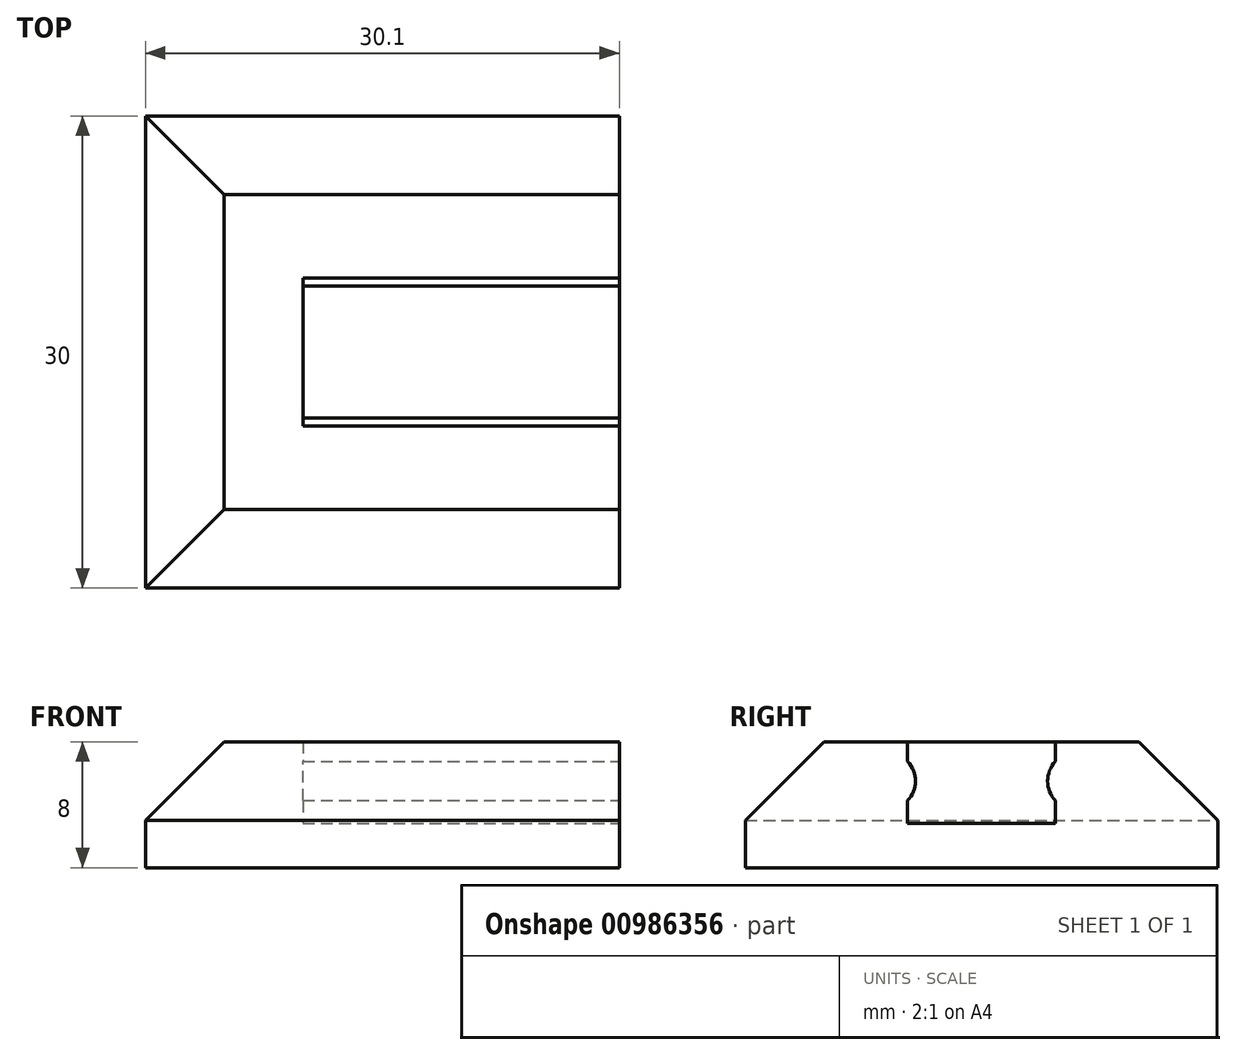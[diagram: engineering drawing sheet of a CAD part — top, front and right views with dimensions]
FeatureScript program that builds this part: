
annotation { "Feature Type Name" : "Feature", "Feature Type Description" : "" }
export const myFeature = defineFeature(function(context is Context, id is Id, definition is map)
    precondition{}
    {
        {
            var Q0;
            Q0=qCreatedBy(makeId("Top.planeOp"),FACE);
            var sketch = newSketch(context, id + "F0", { "sketchPlane" : qUnion([Q0])});
            skLineSegment(sketch, "E0.bottom", {"start": v(63.5, -4.5) * mm, "end": v(-26, -4.5) * mm});
            skLineSegment(sketch, "E0.top", {"start": v(63.5, 4.5) * mm, "end": v(-63.5, 4.5) * mm});
            skLineSegment(sketch, "E0.left", {"start": v(63.5, -4.5) * mm, "end": v(63.5, 4.5) * mm});
            skLineSegment(sketch, "E0.right", {"start": v(-63.5, -4.5) * mm, "end": v(-63.5, 4.5) * mm});
            skPoint(sketch, "E0.middle", {"position": v(0, 0) * mm});
            skLineSegment(sketch, "E1.0", {"start": v(8, 3) * mm, "end": v(-8, 3) * mm});
            skLineSegment(sketch, "E1.1", {"start": v(62, -3) * mm, "end": v(62, 3) * mm});
            skLineSegment(sketch, "E1.2", {"start": v(8, -3) * mm, "end": v(-8, -3) * mm});
            skLineSegment(sketch, "E1.3", {"start": v(-62, -3) * mm, "end": v(-62, 3) * mm});
            skLineSegment(sketch, "E2.left", {"start": v(8, -3) * mm, "end": v(8, 3) * mm, "construction": true});
            skLineSegment(sketch, "E2.right", {"start": v(-8, -3) * mm, "end": v(-8, 3) * mm, "construction": true});
            skLineSegment(sketch, "E3.top", {"start": v(-8, -4.5) * mm, "end": v(-10, -4.5) * mm});
            skLineSegment(sketch, "E3.left", {"start": v(-8, 3) * mm, "end": v(-8, -3) * mm});
            skLineSegment(sketch, "E3.right", {"start": v(-10, 3) * mm, "end": v(-10, -3) * mm});
            skLineSegment(sketch, "E4.top", {"start": v(-10, 4.5) * mm, "end": v(-26, 4.5) * mm, "construction": true});
            skLineSegment(sketch, "E4.left", {"start": v(-10, -3) * mm, "end": v(-10, 3) * mm, "construction": true});
            skLineSegment(sketch, "E4.right", {"start": v(-26, -3) * mm, "end": v(-26, 3) * mm, "construction": true});
            skLineSegment(sketch, "E5.bottom", {"start": v(-26, -4.5) * mm, "end": v(-28, -4.5) * mm});
            skLineSegment(sketch, "E5.top", {"start": v(-26, 4.5) * mm, "end": v(-28, 4.5) * mm});
            skLineSegment(sketch, "E5.left", {"start": v(-26, -3) * mm, "end": v(-26, 3) * mm});
            skLineSegment(sketch, "E5.right", {"start": v(-28, -3) * mm, "end": v(-28, 3) * mm});
            skLineSegment(sketch, "E6.top", {"start": v(-28, 4.5) * mm, "end": v(-44, 4.5) * mm, "construction": true});
            skLineSegment(sketch, "E6.left", {"start": v(-28, -3) * mm, "end": v(-28, 3) * mm, "construction": true});
            skLineSegment(sketch, "E6.right", {"start": v(-44, -3) * mm, "end": v(-44, 3) * mm, "construction": true});
            skLineSegment(sketch, "E7.top", {"start": v(-44, 4.5) * mm, "end": v(-46, 4.5) * mm});
            skLineSegment(sketch, "E7.left", {"start": v(-44, -3) * mm, "end": v(-44, 3) * mm});
            skLineSegment(sketch, "E7.right", {"start": v(-46, -3) * mm, "end": v(-46, 3) * mm});
            skLineSegment(sketch, "E8.top", {"start": v(-46, 4.5) * mm, "end": v(-62, 4.5) * mm, "construction": true});
            skLineSegment(sketch, "E8.left", {"start": v(-46, -3) * mm, "end": v(-46, 3) * mm, "construction": true});
            skLineSegment(sketch, "E8.right", {"start": v(-62, -5) * mm, "end": v(-62, -4.5) * mm, "construction": true});
            skLineSegment(sketch, "E9.trimOffspring", {"start": v(-28, 3) * mm, "end": v(-44, 3) * mm});
            skLineSegment(sketch, "E10.trimOffspring", {"start": v(-46, 3) * mm, "end": v(-62, 3) * mm});
            skLineSegment(sketch, "E11.trimOffspring", {"start": v(-46, -3) * mm, "end": v(-62, -3) * mm});
            skLineSegment(sketch, "E12.trimOffspring", {"start": v(-28, -4.5) * mm, "end": v(-63.5, -4.5) * mm});
            skLineSegment(sketch, "E13.trimOffspring", {"start": v(-28, -3) * mm, "end": v(-44, -3) * mm});
            skLineSegment(sketch, "E14.trimOffspring", {"start": v(-10, 3) * mm, "end": v(-26, 3) * mm});
            skLineSegment(sketch, "E15.trimOffspring", {"start": v(-10, -3) * mm, "end": v(-26, -3) * mm});
            skLineSegment(sketch, "E16", {"start": v(0, 11.85) * mm, "end": v(0, -12.1) * mm, "construction": true});
            skLineSegment(sketch, "E17.MirrorCS", {"start": v(-8, 3) * mm, "end": v(8, 3) * mm});
            skLineSegment(sketch, "E18.MirrorCS", {"start": v(-8, -3) * mm, "end": v(8, -3) * mm});
            skLineSegment(sketch, "E19.MirrorCS", {"start": v(10, -3) * mm, "end": v(10, 3) * mm, "construction": true});
            skLineSegment(sketch, "E20.MirrorCS", {"start": v(10, 3) * mm, "end": v(26, 3) * mm});
            skLineSegment(sketch, "E21.MirrorCS", {"start": v(10, -3) * mm, "end": v(26, -3) * mm});
            skLineSegment(sketch, "E22.MirrorCS", {"start": v(26, -3) * mm, "end": v(26, 3) * mm, "construction": true});
            skLineSegment(sketch, "E23.MirrorCS", {"start": v(28, -3) * mm, "end": v(28, 3) * mm, "construction": true});
            skLineSegment(sketch, "E24.MirrorCS", {"start": v(28, 3) * mm, "end": v(44, 3) * mm});
            skLineSegment(sketch, "E25.MirrorCS", {"start": v(28, -3) * mm, "end": v(44, -3) * mm});
            skLineSegment(sketch, "E26.MirrorCS", {"start": v(46, -3) * mm, "end": v(62, -3) * mm});
            skLineSegment(sketch, "E27.MirrorCS", {"start": v(46, 3) * mm, "end": v(62, 3) * mm});
            skLineSegment(sketch, "E28.MirrorCS", {"start": v(46, -3) * mm, "end": v(46, 3) * mm, "construction": true});
            skLineSegment(sketch, "E29.MirrorCS", {"start": v(44, -3) * mm, "end": v(44, 3) * mm, "construction": true});
            skLineSegment(sketch, "E30", {"start": v(10, 3) * mm, "end": v(10, -3) * mm});
            skLineSegment(sketch, "E31", {"start": v(26, 3) * mm, "end": v(26, -3) * mm});
            skLineSegment(sketch, "E32", {"start": v(28, 3) * mm, "end": v(28, -3) * mm});
            skLineSegment(sketch, "E33", {"start": v(44, 3) * mm, "end": v(44, -3) * mm});
            skLineSegment(sketch, "E34", {"start": v(46, 3) * mm, "end": v(46, -3) * mm});
            skLineSegment(sketch, "E35", {"start": v(8, 3) * mm, "end": v(8, -3) * mm});
            skPoint(sketch, "E36.orphan", {"position": v(-8, -6) * mm});
            skPoint(sketch, "E2.bottom.start.orphan", {"position": v(8, -6) * mm});
            skPoint(sketch, "E37.orphan", {"position": v(8, 6) * mm});
            skPoint(sketch, "E3.bottom.start.orphan", {"position": v(-8, 6) * mm});
            skSolve(sketch);
        }
        {
            var Q0;
            {var subQ6=sQuery(id+"F0.wireOp",EDGE,"E0.left");Q0=makeQuery(id+"F0.imprint","IMPRINT",FACE,{"disambiguationData":[TD([[makeQuery(id+"F0.imprint","IMPRINT",EDGE,{"derivedFrom":subQ6}),1.0]])]});}
            extrude(context, id + "F1", {"entities" : qUnion([Q0]), "depth" : 95 * mm, "offsetDistance" : 25 * mm});
        }
        {
            var Q0;
            Q0=makeQuery(id+"F0.imprint","IMPRINT",FACE,{"disambiguationData":[TD([[makeQuery(id+"F0.imprint","IMPRINT",EDGE,{"derivedFrom":sQuery(id+"F0.wireOp",EDGE,"E1.3")}),-1.0]])]});
            var Q1;
            Q1=makeQuery(id+"F0.imprint","IMPRINT",FACE,{"disambiguationData":[TD([[makeQuery(id+"F0.imprint","IMPRINT",EDGE,{"derivedFrom":sQuery(id+"F0.wireOp",EDGE,"E5.right")}),1.0]])]});
            var Q2;
            {var subQ6=sQuery(id+"F0.wireOp",EDGE,"E0.left");Q2=makeQuery(id+"F0.imprint","IMPRINT",FACE,{"disambiguationData":[TD([[makeQuery(id+"F0.imprint","IMPRINT",EDGE,{"derivedFrom":subQ6}),1.0]])]});}
            var Q3;
            Q3=makeQuery(id+"F0.imprint","IMPRINT",FACE,{"disambiguationData":[TD([[makeQuery(id+"F0.imprint","IMPRINT",EDGE,{"derivedFrom":sQuery(id+"F0.wireOp",EDGE,"E3.right")}),-1.0]])]});
            var Q4;
            Q4=makeQuery(id+"F0.imprint","IMPRINT",FACE,{"disambiguationData":[TD([[makeQuery(id+"F0.imprint","IMPRINT",EDGE,{"derivedFrom":sQuery(id+"F0.wireOp",EDGE,"E3.left")}),1.0]])]});
            var Q5;
            Q5=makeQuery(id+"F0.imprint","IMPRINT",FACE,{"disambiguationData":[TD([[makeQuery(id+"F0.imprint","IMPRINT",EDGE,{"derivedFrom":sQuery(id+"F0.wireOp",EDGE,"E20.MirrorCS")}),-1.0]])]});
            var Q6;
            Q6=makeQuery(id+"F0.imprint","IMPRINT",FACE,{"disambiguationData":[TD([[makeQuery(id+"F0.imprint","IMPRINT",EDGE,{"derivedFrom":sQuery(id+"F0.wireOp",EDGE,"E24.MirrorCS")}),-1.0]])]});
            var Q7;
            Q7=makeQuery(id+"F0.imprint","IMPRINT",FACE,{"disambiguationData":[TD([[makeQuery(id+"F0.imprint","IMPRINT",EDGE,{"derivedFrom":sQuery(id+"F0.wireOp",EDGE,"E26.MirrorCS")}),1.0]])]});
            extrude(context, id + "F2", {"entities" : qUnion([Q0, Q1, Q2, Q3, Q4, Q5, Q6, Q7]), "operationType" : NewBodyOperationType.ADD, "oppositeDirection" : true, "depth" : 5 * mm, "offsetDistance" : 25 * mm});
        }
        {
            var Q0;
            {var subQ0=sQuery(id+"F0.wireOp",EDGE,"E0.right");Q0=makeQuery(id+"F2.boolean.opBoolean","MERGE",FACE,{"derivedFrom":[makeQuery(id+"F1.opExtrude","SWEPT_FACE",FACE,{"disambiguationData":[OSD([subQ0])]}),makeQuery(id+"F2.opExtrude","SWEPT_FACE",FACE,{"disambiguationData":[OSD([subQ0])]})]});}
            var sketch = newSketch(context, id + "F3", { "sketchPlane" : qUnion([Q0])});
            skLineSegment(sketch, "E38", {"start": v(0, 0) * mm, "end": v(0, -7.08) * mm, "construction": true});
            skLineSegment(sketch, "E39", {"start": v(-6.2, -2.5) * mm, "end": v(6.74, -2.5) * mm, "construction": true});
            skCircle(sketch, "E40", {"center": v(-6, -2.5) * mm, "radius": 2 * mm});
            skCircle(sketch, "E41.MirrorC", {"center": v(6, -2.5) * mm, "radius": 2 * mm});
            skSolve(sketch);
        }
        {
            var Q0;
            Q0=qSketchRegion(id+"F3",true);
            extrude(context, id + "F4", {"entities" : qUnion([Q0]), "operationType" : NewBodyOperationType.REMOVE, "endBound" : BoundingType.THROUGH_ALL, "oppositeDirection" : true, "depth" : 25 * mm, "offsetDistance" : 25 * mm});
        }
        {
            var Q0;
            {var subQ0=sQuery(id+"F0.wireOp",EDGE,"E7.top");var subQ1=sQuery(id+"F0.wireOp",EDGE,"E5.top");var subQ2=sQuery(id+"F0.wireOp",EDGE,"E0.top");var subQ3=sQuery(id+"F0.wireOp",EDGE,"E0.right");Q0=makeQuery(id+"F4.boolean.opBoolean","SPLIT",EDGE,{"disambiguationData":[TD([makeQuery(id+"F1.opExtrude","CAP_FACE",FACE,{"disambiguationData":[OSD([sQuery(id+"F0.wireOp",EDGE,"E0.bottom"),subQ2,sQuery(id+"F0.wireOp",EDGE,"E0.left"),subQ3,sQuery(id+"F0.wireOp",EDGE,"E1.3"),sQuery(id+"F0.wireOp",EDGE,"E3.top"),sQuery(id+"F0.wireOp",EDGE,"E3.left"),sQuery(id+"F0.wireOp",EDGE,"E3.right"),sQuery(id+"F0.wireOp",EDGE,"E5.bottom"),subQ1,sQuery(id+"F0.wireOp",EDGE,"E5.left"),sQuery(id+"F0.wireOp",EDGE,"E5.right"),subQ0,sQuery(id+"F0.wireOp",EDGE,"E7.left"),sQuery(id+"F0.wireOp",EDGE,"E7.right"),sQuery(id+"F0.wireOp",EDGE,"E9.trimOffspring"),sQuery(id+"F0.wireOp",EDGE,"E10.trimOffspring"),sQuery(id+"F0.wireOp",EDGE,"E11.trimOffspring"),sQuery(id+"F0.wireOp",EDGE,"E12.trimOffspring"),sQuery(id+"F0.wireOp",EDGE,"E13.trimOffspring"),sQuery(id+"F0.wireOp",EDGE,"E14.trimOffspring"),sQuery(id+"F0.wireOp",EDGE,"E15.trimOffspring"),sQuery(id+"F0.wireOp",EDGE,"E17.MirrorCS"),sQuery(id+"F0.wireOp",EDGE,"E18.MirrorCS"),sQuery(id+"F0.wireOp",EDGE,"E20.MirrorCS"),sQuery(id+"F0.wireOp",EDGE,"E21.MirrorCS"),sQuery(id+"F0.wireOp",EDGE,"E24.MirrorCS"),sQuery(id+"F0.wireOp",EDGE,"E25.MirrorCS"),sQuery(id+"F0.wireOp",EDGE,"E26.MirrorCS"),sQuery(id+"F0.wireOp",EDGE,"E27.MirrorCS"),sQuery(id+"F0.wireOp",EDGE,"E1.1"),sQuery(id+"F0.wireOp",EDGE,"E30"),sQuery(id+"F0.wireOp",EDGE,"E31"),sQuery(id+"F0.wireOp",EDGE,"E32"),sQuery(id+"F0.wireOp",EDGE,"E33"),sQuery(id+"F0.wireOp",EDGE,"E34"),sQuery(id+"F0.wireOp",EDGE,"E35")])],"isStart":false})])],"derivedFrom":makeQuery(id+"F2.boolean.opBoolean","MERGE",EDGE,{"derivedFrom":[makeQuery(id+"F1.opExtrude","SWEPT_EDGE",EDGE,{"disambiguationData":[OSD([subQ2,subQ3])]}),makeQuery(id+"F2.opExtrude","SWEPT_EDGE",EDGE,{"disambiguationData":[OSD([subQ2,subQ3])]})]})});}
            var Q1;
            {var subQ0=sQuery(id+"F0.wireOp",EDGE,"E12.trimOffspring");var subQ1=sQuery(id+"F0.wireOp",EDGE,"E5.bottom");var subQ2=sQuery(id+"F0.wireOp",EDGE,"E3.top");var subQ3=sQuery(id+"F0.wireOp",EDGE,"E0.bottom");var subQ4=sQuery(id+"F0.wireOp",EDGE,"E0.right");Q1=makeQuery(id+"F4.boolean.opBoolean","SPLIT",EDGE,{"disambiguationData":[TD([makeQuery(id+"F1.opExtrude","CAP_FACE",FACE,{"disambiguationData":[OSD([subQ3,sQuery(id+"F0.wireOp",EDGE,"E0.top"),sQuery(id+"F0.wireOp",EDGE,"E0.left"),subQ4,sQuery(id+"F0.wireOp",EDGE,"E1.3"),subQ2,sQuery(id+"F0.wireOp",EDGE,"E3.left"),sQuery(id+"F0.wireOp",EDGE,"E3.right"),subQ1,sQuery(id+"F0.wireOp",EDGE,"E5.top"),sQuery(id+"F0.wireOp",EDGE,"E5.left"),sQuery(id+"F0.wireOp",EDGE,"E5.right"),sQuery(id+"F0.wireOp",EDGE,"E7.top"),sQuery(id+"F0.wireOp",EDGE,"E7.left"),sQuery(id+"F0.wireOp",EDGE,"E7.right"),sQuery(id+"F0.wireOp",EDGE,"E9.trimOffspring"),sQuery(id+"F0.wireOp",EDGE,"E10.trimOffspring"),sQuery(id+"F0.wireOp",EDGE,"E11.trimOffspring"),subQ0,sQuery(id+"F0.wireOp",EDGE,"E13.trimOffspring"),sQuery(id+"F0.wireOp",EDGE,"E14.trimOffspring"),sQuery(id+"F0.wireOp",EDGE,"E15.trimOffspring"),sQuery(id+"F0.wireOp",EDGE,"E17.MirrorCS"),sQuery(id+"F0.wireOp",EDGE,"E18.MirrorCS"),sQuery(id+"F0.wireOp",EDGE,"E20.MirrorCS"),sQuery(id+"F0.wireOp",EDGE,"E21.MirrorCS"),sQuery(id+"F0.wireOp",EDGE,"E24.MirrorCS"),sQuery(id+"F0.wireOp",EDGE,"E25.MirrorCS"),sQuery(id+"F0.wireOp",EDGE,"E26.MirrorCS"),sQuery(id+"F0.wireOp",EDGE,"E27.MirrorCS"),sQuery(id+"F0.wireOp",EDGE,"E1.1"),sQuery(id+"F0.wireOp",EDGE,"E30"),sQuery(id+"F0.wireOp",EDGE,"E31"),sQuery(id+"F0.wireOp",EDGE,"E32"),sQuery(id+"F0.wireOp",EDGE,"E33"),sQuery(id+"F0.wireOp",EDGE,"E34"),sQuery(id+"F0.wireOp",EDGE,"E35")])],"isStart":false})])],"derivedFrom":makeQuery(id+"F2.boolean.opBoolean","MERGE",EDGE,{"derivedFrom":[makeQuery(id+"F1.opExtrude","SWEPT_EDGE",EDGE,{"disambiguationData":[OSD([subQ4,subQ0])]}),makeQuery(id+"F2.opExtrude","SWEPT_EDGE",EDGE,{"disambiguationData":[OSD([subQ4,subQ0])]})]})});}
            var Q2;
            Q2=makeQuery(id+"F2.opExtrude","CAP_EDGE",EDGE,{"disambiguationData":[OSD([sQuery(id+"F0.wireOp",EDGE,"E0.top"),sQuery(id+"F0.wireOp",EDGE,"E5.top"),sQuery(id+"F0.wireOp",EDGE,"E7.top")])],"isStart":false});
            var Q3;
            Q3=makeQuery(id+"F2.opExtrude","CAP_EDGE",EDGE,{"disambiguationData":[OSD([sQuery(id+"F0.wireOp",EDGE,"E0.right")])],"isStart":false});
            var Q4;
            Q4=makeQuery(id+"F4.boolean.opBoolean","COPY",EDGE,{"derivedFrom":makeQuery(id+"F4.opExtrude","CAP_EDGE",EDGE,{"disambiguationData":[OSD([sQuery(id+"F3.wireOp",EDGE,"E40")])],"isStart":true})});
            var Q5;
            Q5=makeQuery(id+"F1.opExtrude","CAP_EDGE",EDGE,{"disambiguationData":[OSD([sQuery(id+"F0.wireOp",EDGE,"E0.top"),sQuery(id+"F0.wireOp",EDGE,"E5.top"),sQuery(id+"F0.wireOp",EDGE,"E7.top")])],"isStart":false});
            var Q6;
            Q6=makeQuery(id+"F1.opExtrude","CAP_EDGE",EDGE,{"disambiguationData":[OSD([sQuery(id+"F0.wireOp",EDGE,"E0.right")])],"isStart":false});
            var Q7;
            Q7=makeQuery(id+"F1.opExtrude","CAP_EDGE",EDGE,{"disambiguationData":[OSD([sQuery(id+"F0.wireOp",EDGE,"E0.bottom"),sQuery(id+"F0.wireOp",EDGE,"E3.top"),sQuery(id+"F0.wireOp",EDGE,"E5.bottom"),sQuery(id+"F0.wireOp",EDGE,"E12.trimOffspring")])],"isStart":false});
            var Q8;
            Q8=makeQuery(id+"F1.opExtrude","CAP_EDGE",EDGE,{"disambiguationData":[OSD([sQuery(id+"F0.wireOp",EDGE,"E0.left")])],"isStart":false});
            var Q9;
            Q9=makeQuery(id+"F2.opExtrude","CAP_EDGE",EDGE,{"disambiguationData":[OSD([sQuery(id+"F0.wireOp",EDGE,"E0.left")])],"isStart":false});
            var Q10;
            {var subQ0=sQuery(id+"F0.wireOp",EDGE,"E7.top");var subQ1=sQuery(id+"F0.wireOp",EDGE,"E5.top");var subQ2=sQuery(id+"F0.wireOp",EDGE,"E0.top");var subQ3=sQuery(id+"F0.wireOp",EDGE,"E0.left");Q10=makeQuery(id+"F4.boolean.opBoolean","SPLIT",EDGE,{"disambiguationData":[TD([makeQuery(id+"F1.opExtrude","CAP_FACE",FACE,{"disambiguationData":[OSD([sQuery(id+"F0.wireOp",EDGE,"E0.bottom"),subQ2,subQ3,sQuery(id+"F0.wireOp",EDGE,"E0.right"),sQuery(id+"F0.wireOp",EDGE,"E1.3"),sQuery(id+"F0.wireOp",EDGE,"E3.top"),sQuery(id+"F0.wireOp",EDGE,"E3.left"),sQuery(id+"F0.wireOp",EDGE,"E3.right"),sQuery(id+"F0.wireOp",EDGE,"E5.bottom"),subQ1,sQuery(id+"F0.wireOp",EDGE,"E5.left"),sQuery(id+"F0.wireOp",EDGE,"E5.right"),subQ0,sQuery(id+"F0.wireOp",EDGE,"E7.left"),sQuery(id+"F0.wireOp",EDGE,"E7.right"),sQuery(id+"F0.wireOp",EDGE,"E9.trimOffspring"),sQuery(id+"F0.wireOp",EDGE,"E10.trimOffspring"),sQuery(id+"F0.wireOp",EDGE,"E11.trimOffspring"),sQuery(id+"F0.wireOp",EDGE,"E12.trimOffspring"),sQuery(id+"F0.wireOp",EDGE,"E13.trimOffspring"),sQuery(id+"F0.wireOp",EDGE,"E14.trimOffspring"),sQuery(id+"F0.wireOp",EDGE,"E15.trimOffspring"),sQuery(id+"F0.wireOp",EDGE,"E17.MirrorCS"),sQuery(id+"F0.wireOp",EDGE,"E18.MirrorCS"),sQuery(id+"F0.wireOp",EDGE,"E20.MirrorCS"),sQuery(id+"F0.wireOp",EDGE,"E21.MirrorCS"),sQuery(id+"F0.wireOp",EDGE,"E24.MirrorCS"),sQuery(id+"F0.wireOp",EDGE,"E25.MirrorCS"),sQuery(id+"F0.wireOp",EDGE,"E26.MirrorCS"),sQuery(id+"F0.wireOp",EDGE,"E27.MirrorCS"),sQuery(id+"F0.wireOp",EDGE,"E1.1"),sQuery(id+"F0.wireOp",EDGE,"E30"),sQuery(id+"F0.wireOp",EDGE,"E31"),sQuery(id+"F0.wireOp",EDGE,"E32"),sQuery(id+"F0.wireOp",EDGE,"E33"),sQuery(id+"F0.wireOp",EDGE,"E34"),sQuery(id+"F0.wireOp",EDGE,"E35")])],"isStart":false})])],"derivedFrom":makeQuery(id+"F2.boolean.opBoolean","MERGE",EDGE,{"derivedFrom":[makeQuery(id+"F1.opExtrude","SWEPT_EDGE",EDGE,{"disambiguationData":[OSD([subQ2,subQ3])]}),makeQuery(id+"F2.opExtrude","SWEPT_EDGE",EDGE,{"disambiguationData":[OSD([subQ2,subQ3])]})]})});}
            var Q11;
            {var subQ0=sQuery(id+"F0.wireOp",EDGE,"E12.trimOffspring");var subQ1=sQuery(id+"F0.wireOp",EDGE,"E5.bottom");var subQ2=sQuery(id+"F0.wireOp",EDGE,"E3.top");var subQ3=sQuery(id+"F0.wireOp",EDGE,"E0.bottom");var subQ4=sQuery(id+"F0.wireOp",EDGE,"E0.left");Q11=makeQuery(id+"F4.boolean.opBoolean","SPLIT",EDGE,{"disambiguationData":[TD([makeQuery(id+"F1.opExtrude","CAP_FACE",FACE,{"disambiguationData":[OSD([subQ3,sQuery(id+"F0.wireOp",EDGE,"E0.top"),subQ4,sQuery(id+"F0.wireOp",EDGE,"E0.right"),sQuery(id+"F0.wireOp",EDGE,"E1.3"),subQ2,sQuery(id+"F0.wireOp",EDGE,"E3.left"),sQuery(id+"F0.wireOp",EDGE,"E3.right"),subQ1,sQuery(id+"F0.wireOp",EDGE,"E5.top"),sQuery(id+"F0.wireOp",EDGE,"E5.left"),sQuery(id+"F0.wireOp",EDGE,"E5.right"),sQuery(id+"F0.wireOp",EDGE,"E7.top"),sQuery(id+"F0.wireOp",EDGE,"E7.left"),sQuery(id+"F0.wireOp",EDGE,"E7.right"),sQuery(id+"F0.wireOp",EDGE,"E9.trimOffspring"),sQuery(id+"F0.wireOp",EDGE,"E10.trimOffspring"),sQuery(id+"F0.wireOp",EDGE,"E11.trimOffspring"),subQ0,sQuery(id+"F0.wireOp",EDGE,"E13.trimOffspring"),sQuery(id+"F0.wireOp",EDGE,"E14.trimOffspring"),sQuery(id+"F0.wireOp",EDGE,"E15.trimOffspring"),sQuery(id+"F0.wireOp",EDGE,"E17.MirrorCS"),sQuery(id+"F0.wireOp",EDGE,"E18.MirrorCS"),sQuery(id+"F0.wireOp",EDGE,"E20.MirrorCS"),sQuery(id+"F0.wireOp",EDGE,"E21.MirrorCS"),sQuery(id+"F0.wireOp",EDGE,"E24.MirrorCS"),sQuery(id+"F0.wireOp",EDGE,"E25.MirrorCS"),sQuery(id+"F0.wireOp",EDGE,"E26.MirrorCS"),sQuery(id+"F0.wireOp",EDGE,"E27.MirrorCS"),sQuery(id+"F0.wireOp",EDGE,"E1.1"),sQuery(id+"F0.wireOp",EDGE,"E30"),sQuery(id+"F0.wireOp",EDGE,"E31"),sQuery(id+"F0.wireOp",EDGE,"E32"),sQuery(id+"F0.wireOp",EDGE,"E33"),sQuery(id+"F0.wireOp",EDGE,"E34"),sQuery(id+"F0.wireOp",EDGE,"E35")])],"isStart":false})])],"derivedFrom":makeQuery(id+"F2.boolean.opBoolean","MERGE",EDGE,{"derivedFrom":[makeQuery(id+"F1.opExtrude","SWEPT_EDGE",EDGE,{"disambiguationData":[OSD([subQ3,subQ4])]}),makeQuery(id+"F2.opExtrude","SWEPT_EDGE",EDGE,{"disambiguationData":[OSD([subQ3,subQ4])]})]})});}
            var Q12;
            Q12=makeQuery(id+"F4.boolean.opBoolean","COPY",EDGE,{"derivedFrom":makeQuery(id+"F4.opExtrude","CAP_EDGE",EDGE,{"disambiguationData":[OSD([sQuery(id+"F3.wireOp",EDGE,"E41.MirrorC")])],"isStart":true})});
            var Q13;
            {var subQ0=sQuery(id+"F0.wireOp",EDGE,"E0.left");Q13=makeQuery(id+"F4.boolean.opBoolean","INTERSECT",EDGE,{"derivedFrom":[makeQuery(id+"F2.boolean.opBoolean","MERGE",FACE,{"derivedFrom":[makeQuery(id+"F1.opExtrude","SWEPT_FACE",FACE,{"disambiguationData":[OSD([subQ0])]}),makeQuery(id+"F2.opExtrude","SWEPT_FACE",FACE,{"disambiguationData":[OSD([subQ0])]})]}),makeQuery(id+"F4.opExtrude","SWEPT_FACE",FACE,{"disambiguationData":[OSD([sQuery(id+"F3.wireOp",EDGE,"E40")])]})]});}
            var Q14;
            {var subQ0=sQuery(id+"F0.wireOp",EDGE,"E0.left");Q14=makeQuery(id+"F4.boolean.opBoolean","INTERSECT",EDGE,{"derivedFrom":[makeQuery(id+"F2.boolean.opBoolean","MERGE",FACE,{"derivedFrom":[makeQuery(id+"F1.opExtrude","SWEPT_FACE",FACE,{"disambiguationData":[OSD([subQ0])]}),makeQuery(id+"F2.opExtrude","SWEPT_FACE",FACE,{"disambiguationData":[OSD([subQ0])]})]}),makeQuery(id+"F4.opExtrude","SWEPT_FACE",FACE,{"disambiguationData":[OSD([sQuery(id+"F3.wireOp",EDGE,"E41.MirrorC")])]})]});}
            var Q15;
            Q15=makeQuery(id+"F1.opExtrude","CAP_EDGE",EDGE,{"disambiguationData":[OSD([sQuery(id+"F0.wireOp",EDGE,"E26.MirrorCS")])],"isStart":false});
            var Q16;
            Q16=makeQuery(id+"F1.opExtrude","CAP_EDGE",EDGE,{"disambiguationData":[OSD([sQuery(id+"F0.wireOp",EDGE,"E34")])],"isStart":false});
            var Q17;
            Q17=makeQuery(id+"F1.opExtrude","CAP_EDGE",EDGE,{"disambiguationData":[OSD([sQuery(id+"F0.wireOp",EDGE,"E27.MirrorCS")])],"isStart":false});
            var Q18;
            Q18=makeQuery(id+"F1.opExtrude","CAP_EDGE",EDGE,{"disambiguationData":[OSD([sQuery(id+"F0.wireOp",EDGE,"E1.1")])],"isStart":false});
            var Q19;
            Q19=makeQuery(id+"F1.opExtrude","CAP_EDGE",EDGE,{"disambiguationData":[OSD([sQuery(id+"F0.wireOp",EDGE,"E33")])],"isStart":false});
            var Q20;
            Q20=makeQuery(id+"F1.opExtrude","CAP_EDGE",EDGE,{"disambiguationData":[OSD([sQuery(id+"F0.wireOp",EDGE,"E24.MirrorCS")])],"isStart":false});
            var Q21;
            Q21=makeQuery(id+"F1.opExtrude","CAP_EDGE",EDGE,{"disambiguationData":[OSD([sQuery(id+"F0.wireOp",EDGE,"E25.MirrorCS")])],"isStart":false});
            var Q22;
            Q22=makeQuery(id+"F1.opExtrude","CAP_EDGE",EDGE,{"disambiguationData":[OSD([sQuery(id+"F0.wireOp",EDGE,"E35")])],"isStart":false});
            var Q23;
            Q23=makeQuery(id+"F1.opExtrude","CAP_EDGE",EDGE,{"disambiguationData":[OSD([sQuery(id+"F0.wireOp",EDGE,"E30")])],"isStart":false});
            var Q24;
            Q24=makeQuery(id+"F1.opExtrude","CAP_EDGE",EDGE,{"disambiguationData":[OSD([sQuery(id+"F0.wireOp",EDGE,"E20.MirrorCS")])],"isStart":false});
            var Q25;
            Q25=makeQuery(id+"F1.opExtrude","CAP_EDGE",EDGE,{"disambiguationData":[OSD([sQuery(id+"F0.wireOp",EDGE,"E21.MirrorCS")])],"isStart":false});
            var Q26;
            Q26=makeQuery(id+"F1.opExtrude","CAP_EDGE",EDGE,{"disambiguationData":[OSD([sQuery(id+"F0.wireOp",EDGE,"E31")])],"isStart":false});
            var Q27;
            Q27=makeQuery(id+"F1.opExtrude","CAP_EDGE",EDGE,{"disambiguationData":[OSD([sQuery(id+"F0.wireOp",EDGE,"E32")])],"isStart":false});
            var Q28;
            Q28=makeQuery(id+"F1.opExtrude","CAP_EDGE",EDGE,{"disambiguationData":[OSD([sQuery(id+"F0.wireOp",EDGE,"E17.MirrorCS")])],"isStart":false});
            var Q29;
            Q29=makeQuery(id+"F1.opExtrude","CAP_EDGE",EDGE,{"disambiguationData":[OSD([sQuery(id+"F0.wireOp",EDGE,"E18.MirrorCS")])],"isStart":false});
            var Q30;
            Q30=makeQuery(id+"F1.opExtrude","CAP_EDGE",EDGE,{"disambiguationData":[OSD([sQuery(id+"F0.wireOp",EDGE,"E3.left")])],"isStart":false});
            var Q31;
            Q31=makeQuery(id+"F1.opExtrude","CAP_EDGE",EDGE,{"disambiguationData":[OSD([sQuery(id+"F0.wireOp",EDGE,"E3.right")])],"isStart":false});
            var Q32;
            Q32=makeQuery(id+"F1.opExtrude","CAP_EDGE",EDGE,{"disambiguationData":[OSD([sQuery(id+"F0.wireOp",EDGE,"E15.trimOffspring")])],"isStart":false});
            var Q33;
            Q33=makeQuery(id+"F1.opExtrude","CAP_EDGE",EDGE,{"disambiguationData":[OSD([sQuery(id+"F0.wireOp",EDGE,"E5.left")])],"isStart":false});
            var Q34;
            Q34=makeQuery(id+"F1.opExtrude","CAP_EDGE",EDGE,{"disambiguationData":[OSD([sQuery(id+"F0.wireOp",EDGE,"E14.trimOffspring")])],"isStart":false});
            var Q35;
            Q35=makeQuery(id+"F1.opExtrude","CAP_EDGE",EDGE,{"disambiguationData":[OSD([sQuery(id+"F0.wireOp",EDGE,"E9.trimOffspring")])],"isStart":false});
            var Q36;
            Q36=makeQuery(id+"F1.opExtrude","CAP_EDGE",EDGE,{"disambiguationData":[OSD([sQuery(id+"F0.wireOp",EDGE,"E5.right")])],"isStart":false});
            var Q37;
            Q37=makeQuery(id+"F1.opExtrude","CAP_EDGE",EDGE,{"disambiguationData":[OSD([sQuery(id+"F0.wireOp",EDGE,"E13.trimOffspring")])],"isStart":false});
            var Q38;
            Q38=makeQuery(id+"F1.opExtrude","CAP_EDGE",EDGE,{"disambiguationData":[OSD([sQuery(id+"F0.wireOp",EDGE,"E10.trimOffspring")])],"isStart":false});
            var Q39;
            Q39=makeQuery(id+"F1.opExtrude","CAP_EDGE",EDGE,{"disambiguationData":[OSD([sQuery(id+"F0.wireOp",EDGE,"E1.3")])],"isStart":false});
            var Q40;
            Q40=makeQuery(id+"F1.opExtrude","CAP_EDGE",EDGE,{"disambiguationData":[OSD([sQuery(id+"F0.wireOp",EDGE,"E11.trimOffspring")])],"isStart":false});
            var Q41;
            Q41=makeQuery(id+"F1.opExtrude","CAP_EDGE",EDGE,{"disambiguationData":[OSD([sQuery(id+"F0.wireOp",EDGE,"E7.right")])],"isStart":false});
            var Q42;
            Q42=makeQuery(id+"F1.opExtrude","CAP_EDGE",EDGE,{"disambiguationData":[OSD([sQuery(id+"F0.wireOp",EDGE,"E7.left")])],"isStart":false});
            chamfer(context, id + "F5", {"entities" : qUnion([Q0, Q1, Q2, Q3, Q4, Q5, Q6, Q7, Q8, Q9, Q10, Q11, Q12, Q13, Q14, Q15, Q16, Q17, Q18, Q19, Q20, Q21, Q22, Q23, Q24, Q25, Q26, Q27, Q28, Q29, Q30, Q31, Q32, Q33, Q34, Q35, Q36, Q37, Q38, Q39, Q40, Q41, Q42]), "width" : 0.5 * mm, "tangentPropagation" : true});
        }
        {
            var Q0;
            {var subQ0=sQuery(id+"F0.wireOp",EDGE,"E0.right");var subQ2=makeQuery(id+"F1.opExtrude","CAP_EDGE",EDGE,{"disambiguationData":[OSD([subQ0])],"isStart":false});Q0=makeQuery(id+"F3.imprint","IMPRINT",FACE,{"disambiguationData":[TD([[makeQuery(id+"F3.imprint","IMPRINT",EDGE,{"derivedFrom":subQ2}),1.0]])]});}
            extrude(context, id + "F6", {"entities" : qUnion([Q0]), "operationType" : NewBodyOperationType.ADD, "depth" : 25 * mm, "offsetDistance" : 25 * mm});
        }
        {
            var Q0;
            Q0=makeQuery(id+"F6.opExtrude","CAP_FACE",FACE,{"disambiguationData":[OSD([sQuery(id+"F0.wireOp",EDGE,"E0.top"),sQuery(id+"F0.wireOp",EDGE,"E0.right"),sQuery(id+"F0.wireOp",EDGE,"E12.trimOffspring"),sQuery(id+"F3.wireOp",EDGE,"E40"),sQuery(id+"F3.wireOp",EDGE,"E41.MirrorC")])],"isStart":false});
            var sketch = newSketch(context, id + "F7", { "sketchPlane" : qUnion([Q0])});
            skLineSegment(sketch, "E42.0", {"start": v(4.7, 0) * mm, "end": v(4.7, -1.26) * mm});
            skArc(sketch, "E42.1", {"start": v(4.7, -3.74) * mm, "mid": v(4.2, -2.5) * mm, "end": v(4.7, -1.26) * mm});
            skLineSegment(sketch, "E42.2", {"start": v(4.7, -3.74) * mm, "end": v(4.7, -5.2) * mm});
            skLineSegment(sketch, "E42.3", {"start": v(-4.7, 0) * mm, "end": v(-4.7, -1.26) * mm});
            skArc(sketch, "E42.4", {"start": v(-4.7, -3.74) * mm, "mid": v(-4.2, -2.5) * mm, "end": v(-4.7, -1.26) * mm});
            skLineSegment(sketch, "E42.5", {"start": v(-4.7, -3.74) * mm, "end": v(-4.7, -5.2) * mm});
            skLineSegment(sketch, "E42.6", {"start": v(4.7, -5.2) * mm, "end": v(-4.7, -5.2) * mm});
            skLineSegment(sketch, "E43.bottom", {"start": v(15, 0) * mm, "end": v(4.7, 0) * mm});
            skLineSegment(sketch, "E43.left", {"start": v(15, 0) * mm, "end": v(15, -8) * mm});
            skLineSegment(sketch, "E43.right", {"start": v(-15, 0) * mm, "end": v(-15, -8) * mm});
            skPoint(sketch, "E43.middle", {"position": v(0, -5) * mm});
            skPoint(sketch, "E44", {"position": v(4.7, 0) * mm});
            skPoint(sketch, "E45", {"position": v(-4.7, 0) * mm});
            skLineSegment(sketch, "E46.trimOffspring", {"start": v(-4.7, 0) * mm, "end": v(-15, 0) * mm});
            skLineSegment(sketch, "E47", {"start": v(-15, -8) * mm, "end": v(15, -8) * mm});
            skPoint(sketch, "E43.top.start.orphan", {"position": v(15, -10) * mm});
            skPoint(sketch, "E48.orphan", {"position": v(-15, -10) * mm});
            skSolve(sketch);
        }
        {
            var Q0;
            Q0=makeQuery(id+"F7.imprint","IMPRINT",FACE,{"disambiguationData":[TD([[makeQuery(id+"F7.imprint","IMPRINT",EDGE,{"derivedFrom":sQuery(id+"F7.wireOp",EDGE,"E42.0")}),1.0]])]});
            extrude(context, id + "F8", {"entities" : qUnion([Q0]), "depth" : 25 * mm, "offsetDistance" : 25 * mm});
        }
        {
            var Q0;
            {var subQ0=sQuery(id+"F0.wireOp",EDGE,"E0.right");var subQ1=sQuery(id+"F0.wireOp",EDGE,"E0.top");var subQ2=makeQuery(id+"F2.boolean.opBoolean","MERGE",EDGE,{"derivedFrom":[makeQuery(id+"F1.opExtrude","SWEPT_EDGE",EDGE,{"disambiguationData":[OSD([subQ1,subQ0])]}),makeQuery(id+"F2.opExtrude","SWEPT_EDGE",EDGE,{"disambiguationData":[OSD([subQ1,subQ0])]})]});Q0=makeQuery(id+"F6.opExtrude","SWEPT_FACE",FACE,{"disambiguationData":[OSD([subQ1,subQ0]),TDD([makeQuery(id+"F3.imprint","IMPRINT",EDGE,{"disambiguationData":[TD([[makeQuery(id+"F3.imprint","INTERSECT",VERTEX,{"derivedFrom":[makeQuery(id+"F1.opExtrude","CAP_EDGE",EDGE,{"disambiguationData":[OSD([subQ0])],"isStart":false}),subQ2]}),-1.0]])],"derivedFrom":subQ2})])]});}
            var sketch = newSketch(context, id + "F9", { "sketchPlane" : qUnion([Q0])});
            skLineSegment(sketch, "E49.bottom", {"start": v(90.96, -21.32) * mm, "end": v(-227.64, -21.32) * mm});
            skLineSegment(sketch, "E49.top", {"start": v(90.96, 221.98) * mm, "end": v(-227.64, 221.98) * mm});
            skLineSegment(sketch, "E49.left", {"start": v(90.96, -21.32) * mm, "end": v(90.96, 221.98) * mm});
            skLineSegment(sketch, "E49.right", {"start": v(-227.64, -21.32) * mm, "end": v(-227.64, 221.98) * mm});
            skPoint(sketch, "E49.middle", {"position": v(-68.34, 100.33) * mm});
            skSolve(sketch);
        }
        {
            var Q0;
            Q0 = qSketchRegion(id + "F9", true);
            extrude(context, id + "F10", {"entities" : qUnion([Q0]), "operationType" : NewBodyOperationType.REMOVE, "endBound" : BoundingType.THROUGH_ALL, "oppositeDirection" : true, "depth" : 25 * mm, "offsetDistance" : 25 * mm});
        }
        {
            var Q0;
            Q0=makeQuery(id+"F8.opExtrude","CAP_FACE",FACE,{"disambiguationData":[OSD([sQuery(id+"F7.wireOp",EDGE,"E42.0"),sQuery(id+"F7.wireOp",EDGE,"E42.1"),sQuery(id+"F7.wireOp",EDGE,"E42.2"),sQuery(id+"F7.wireOp",EDGE,"E42.3"),sQuery(id+"F7.wireOp",EDGE,"E42.4"),sQuery(id+"F7.wireOp",EDGE,"E42.5"),sQuery(id+"F7.wireOp",EDGE,"E42.6"),sQuery(id+"F7.wireOp",EDGE,"E43.bottom"),sQuery(id+"F7.wireOp",EDGE,"E43.left"),sQuery(id+"F7.wireOp",EDGE,"E43.right"),sQuery(id+"F7.wireOp",EDGE,"E46.trimOffspring"),sQuery(id+"F7.wireOp",EDGE,"E47")])],"isStart":false});
            var sketch = newSketch(context, id + "F11", { "sketchPlane" : qUnion([Q0])});
            skLineSegment(sketch, "E50", {"start": v(-4.7, 0) * mm, "end": v(4.7, 0) * mm});
            skSolve(sketch);
        }
        {
            var Q0;
            Q0=makeQuery(id+"F11.imprint","IMPRINT",FACE,{"disambiguationData":[TD([[makeQuery(id+"F11.imprint","IMPRINT",EDGE,{"derivedFrom":makeQuery(id+"F8.opExtrude","CAP_EDGE",EDGE,{"disambiguationData":[OSD([sQuery(id+"F7.wireOp",EDGE,"E42.0")])],"isStart":false})}),1.0]])]});
            var Q1;
            Q1=makeQuery(id+"F11.imprint","IMPRINT",FACE,{"disambiguationData":[TD([[makeQuery(id+"F11.imprint","IMPRINT",EDGE,{"derivedFrom":sQuery(id+"F11.wireOp",EDGE,"E50")}),-1.0]])]});
            extrude(context, id + "F12", {"entities" : qUnion([Q0, Q1]), "operationType" : NewBodyOperationType.ADD, "depth" : 10 * mm, "offsetDistance" : 25 * mm});
        }
        {
            var Q0;
            {var subQ0=sQuery(id+"F7.wireOp",EDGE,"E47");Q0=makeQuery(id+"F12.boolean.opBoolean","MERGE",FACE,{"derivedFrom":[makeQuery(id+"F8.opExtrude","SWEPT_FACE",FACE,{"disambiguationData":[OSD([subQ0])]}),makeQuery(id+"F12.opExtrude","SWEPT_FACE",FACE,{"disambiguationData":[OSD([subQ0])]})]});}
            var sketch = newSketch(context, id + "F13", { "sketchPlane" : qUnion([Q0])});
            skLineSegment(sketch, "E51.bottom", {"start": v(-75.37, -19.61) * mm, "end": v(-93.4, -19.61) * mm});
            skLineSegment(sketch, "E51.top", {"start": v(-75.37, 58) * mm, "end": v(-93.4, 58) * mm});
            skLineSegment(sketch, "E51.left", {"start": v(-75.37, -19.61) * mm, "end": v(-75.37, 58) * mm});
            skLineSegment(sketch, "E51.right", {"start": v(-93.4, -19.61) * mm, "end": v(-93.4, 58) * mm});
            skPoint(sketch, "E51.middle", {"position": v(-84.38, 19.2) * mm});
            skSolve(sketch);
        }
        {
            var Q0;
            {var subQ1=sQuery(id+"F13.wireOp",EDGE,"E51.bottom");Q0=makeQuery(id+"F13.imprint","IMPRINT",FACE,{"disambiguationData":[TD([[makeQuery(id+"F13.imprint","IMPRINT",EDGE,{"derivedFrom":subQ1}),-1.0]])]});}
            var Q1;
            {var subQ1=sQuery(id+"F7.wireOp",EDGE,"E47");var subQ4=makeQuery(id+"F8.opExtrude","CAP_EDGE",EDGE,{"disambiguationData":[OSD([subQ1])],"isStart":true});Q1=makeQuery(id+"F13.imprint","IMPRINT",FACE,{"disambiguationData":[TD([[makeQuery(id+"F13.imprint","IMPRINT",EDGE,{"derivedFrom":subQ4}),1.0]])]});}
            extrude(context, id + "F14", {"entities" : qUnion([Q0, Q1]), "operationType" : NewBodyOperationType.REMOVE, "endBound" : BoundingType.THROUGH_ALL, "oppositeDirection" : true, "depth" : 25 * mm, "offsetDistance" : 25 * mm});
        }
        {
            var Q0;
            {var subQ0=sQuery(id+"F7.wireOp",EDGE,"E46.trimOffspring");var subQ1=sQuery(id+"F7.wireOp",EDGE,"E43.right");Q0=makeQuery(id+"F12.boolean.opBoolean","MERGE",EDGE,{"derivedFrom":[makeQuery(id+"F8.opExtrude","SWEPT_EDGE",EDGE,{"disambiguationData":[OSD([subQ1,subQ0])]}),makeQuery(id+"F12.opExtrude","SWEPT_EDGE",EDGE,{"disambiguationData":[OSD([subQ1,subQ0])]})]});}
            var Q1;
            {var subQ0=sQuery(id+"F7.wireOp",EDGE,"E43.left");var subQ1=sQuery(id+"F7.wireOp",EDGE,"E43.bottom");Q1=makeQuery(id+"F12.boolean.opBoolean","MERGE",EDGE,{"derivedFrom":[makeQuery(id+"F8.opExtrude","SWEPT_EDGE",EDGE,{"disambiguationData":[OSD([subQ1,subQ0])]}),makeQuery(id+"F12.opExtrude","SWEPT_EDGE",EDGE,{"disambiguationData":[OSD([subQ1,subQ0])]})]});}
            chamfer(context, id + "F15", {"entities" : qUnion([Q0, Q1]), "width" : 5 * mm, "tangentPropagation" : true});
        }
        {
            var Q0;
            Q0=makeQuery(id+"F12.opExtrude","CAP_EDGE",EDGE,{"disambiguationData":[OSD([sQuery(id+"F7.wireOp",EDGE,"E43.bottom"),sQuery(id+"F7.wireOp",EDGE,"E46.trimOffspring"),sQuery(id+"F11.wireOp",EDGE,"E50")])],"isStart":false});
            chamfer(context, id + "F16", {"entities" : qUnion([Q0]), "width" : 5 * mm, "tangentPropagation" : true});
        }
    });
